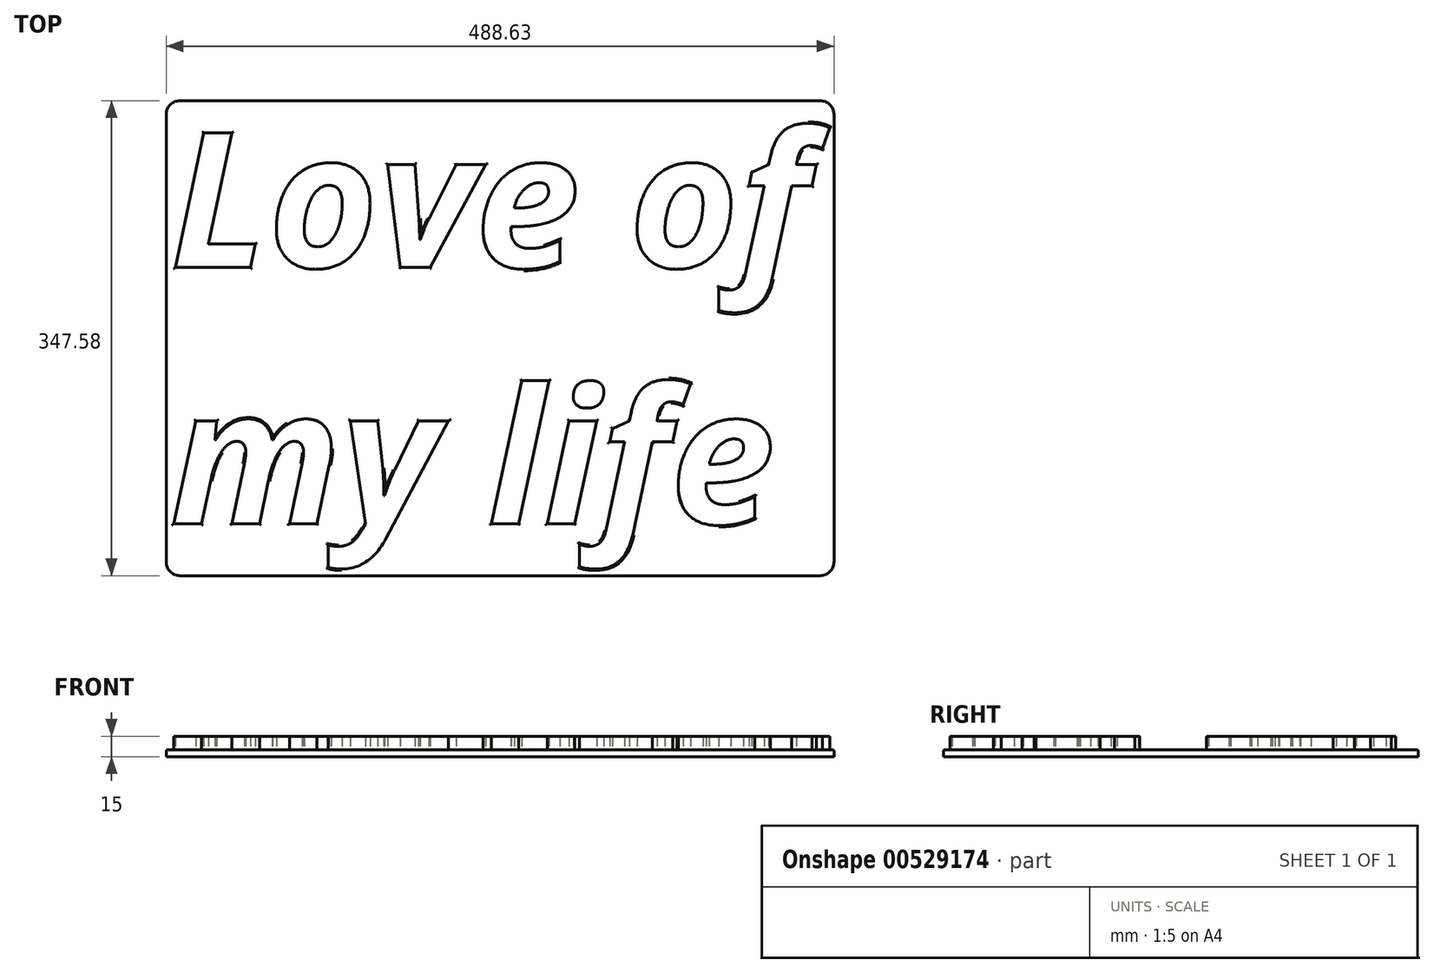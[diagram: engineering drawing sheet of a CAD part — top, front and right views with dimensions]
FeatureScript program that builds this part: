
annotation { "Feature Type Name" : "Feature", "Feature Type Description" : "" }
export const myFeature = defineFeature(function(context is Context, id is Id, definition is map)
    precondition{}
    {
        {
            var Q0;
            Q0=qCreatedBy(makeId("Top.planeOp"),FACE);
            var sketch = newSketch(context, id + "F0", { "sketchPlane" : qUnion([Q0])});
            skText(sketch, "E0", { "text": "Love of \nmy life", "fontName": "OpenSans-BoldItalic.ttf"});
            const initialGuessF0  = {"E0": [-0.07003, -0.04766, 1, 0, 0.09928]};
            skSetInitialGuess(sketch, initialGuessF0);
            skSolve(sketch);
        }
        {
            var Q0;
            Q0 = qSketchRegion(id + "F0", true);
            extrude(context, id + "F1", {"entities" : qUnion([Q0]), "depth" : 10 * mm, "offsetDistance" : 25 * mm});
        }
        {
            var Q0;
            Q0=qCreatedBy(makeId("Top.planeOp"),FACE);
            var sketch = newSketch(context, id + "F2", { "sketchPlane" : qUnion([Q0])});
            skLineSegment(sketch, "E1.bottom", {"start": v(-73.16, 74.37) * mm, "end": v(415.47, 74.37) * mm});
            skLineSegment(sketch, "E1.top", {"start": v(-73.16, -273.2) * mm, "end": v(415.47, -273.2) * mm});
            skLineSegment(sketch, "E1.left", {"start": v(-73.16, 74.37) * mm, "end": v(-73.16, -273.2) * mm});
            skLineSegment(sketch, "E1.right", {"start": v(415.47, 74.37) * mm, "end": v(415.47, -273.2) * mm});
            skSolve(sketch);
        }
        {
            var Q0;
            Q0 = qSketchRegion(id + "F2", true);
            extrude(context, id + "F3", {"entities" : qUnion([Q0]), "oppositeDirection" : true, "depth" : 5 * mm, "offsetDistance" : 25 * mm});
        }
        {
            var Q0;
            Q0=makeQuery(id+"F1.opExtrude","SWEPT_BODY",BODY,{"disambiguationData":[OSD([sQuery(id+"F0.wireOp",EDGE,"E0.sketch_text.stroke-0"),sQuery(id+"F0.wireOp",EDGE,"E0.sketch_text.stroke-1"),sQuery(id+"F0.wireOp",EDGE,"E0.sketch_text.stroke-2"),sQuery(id+"F0.wireOp",EDGE,"E0.sketch_text.stroke-3"),sQuery(id+"F0.wireOp",EDGE,"E0.sketch_text.stroke-4"),sQuery(id+"F0.wireOp",EDGE,"E0.sketch_text.stroke-5")])]});
            var Q1;
            Q1=makeQuery(id+"F1.opExtrude","SWEPT_BODY",BODY,{"disambiguationData":[OSD([sQuery(id+"F0.wireOp",EDGE,"E0.sketch_text.stroke-6"),sQuery(id+"F0.wireOp",EDGE,"E0.sketch_text.stroke-7"),sQuery(id+"F0.wireOp",EDGE,"E0.sketch_text.stroke-8"),sQuery(id+"F0.wireOp",EDGE,"E0.sketch_text.stroke-9"),sQuery(id+"F0.wireOp",EDGE,"E0.sketch_text.stroke-10"),sQuery(id+"F0.wireOp",EDGE,"E0.sketch_text.stroke-11"),sQuery(id+"F0.wireOp",EDGE,"E0.sketch_text.stroke-12"),sQuery(id+"F0.wireOp",EDGE,"E0.sketch_text.stroke-13"),sQuery(id+"F0.wireOp",EDGE,"E0.sketch_text.stroke-14"),sQuery(id+"F0.wireOp",EDGE,"E0.sketch_text.stroke-15"),sQuery(id+"F0.wireOp",EDGE,"E0.sketch_text.stroke-16"),sQuery(id+"F0.wireOp",EDGE,"E0.sketch_text.stroke-17"),sQuery(id+"F0.wireOp",EDGE,"E0.sketch_text.stroke-18"),sQuery(id+"F0.wireOp",EDGE,"E0.sketch_text.stroke-19"),sQuery(id+"F0.wireOp",EDGE,"E0.sketch_text.stroke-20"),sQuery(id+"F0.wireOp",EDGE,"E0.sketch_text.stroke-21"),sQuery(id+"F0.wireOp",EDGE,"E0.sketch_text.stroke-22"),sQuery(id+"F0.wireOp",EDGE,"E0.sketch_text.stroke-23")])]});
            var Q2;
            Q2=makeQuery(id+"F1.opExtrude","SWEPT_BODY",BODY,{"disambiguationData":[OSD([sQuery(id+"F0.wireOp",EDGE,"E0.sketch_text.stroke-24"),sQuery(id+"F0.wireOp",EDGE,"E0.sketch_text.stroke-25"),sQuery(id+"F0.wireOp",EDGE,"E0.sketch_text.stroke-26"),sQuery(id+"F0.wireOp",EDGE,"E0.sketch_text.stroke-27"),sQuery(id+"F0.wireOp",EDGE,"E0.sketch_text.stroke-28"),sQuery(id+"F0.wireOp",EDGE,"E0.sketch_text.stroke-29"),sQuery(id+"F0.wireOp",EDGE,"E0.sketch_text.stroke-30"),sQuery(id+"F0.wireOp",EDGE,"E0.sketch_text.stroke-31"),sQuery(id+"F0.wireOp",EDGE,"E0.sketch_text.stroke-32"),sQuery(id+"F0.wireOp",EDGE,"E0.sketch_text.stroke-33")])]});
            var Q3;
            Q3=makeQuery(id+"F1.opExtrude","SWEPT_BODY",BODY,{"disambiguationData":[OSD([sQuery(id+"F0.wireOp",EDGE,"E0.sketch_text.stroke-34"),sQuery(id+"F0.wireOp",EDGE,"E0.sketch_text.stroke-35"),sQuery(id+"F0.wireOp",EDGE,"E0.sketch_text.stroke-36"),sQuery(id+"F0.wireOp",EDGE,"E0.sketch_text.stroke-37"),sQuery(id+"F0.wireOp",EDGE,"E0.sketch_text.stroke-38"),sQuery(id+"F0.wireOp",EDGE,"E0.sketch_text.stroke-39"),sQuery(id+"F0.wireOp",EDGE,"E0.sketch_text.stroke-40"),sQuery(id+"F0.wireOp",EDGE,"E0.sketch_text.stroke-41"),sQuery(id+"F0.wireOp",EDGE,"E0.sketch_text.stroke-42"),sQuery(id+"F0.wireOp",EDGE,"E0.sketch_text.stroke-43"),sQuery(id+"F0.wireOp",EDGE,"E0.sketch_text.stroke-44"),sQuery(id+"F0.wireOp",EDGE,"E0.sketch_text.stroke-45"),sQuery(id+"F0.wireOp",EDGE,"E0.sketch_text.stroke-46"),sQuery(id+"F0.wireOp",EDGE,"E0.sketch_text.stroke-47"),sQuery(id+"F0.wireOp",EDGE,"E0.sketch_text.stroke-48"),sQuery(id+"F0.wireOp",EDGE,"E0.sketch_text.stroke-49"),sQuery(id+"F0.wireOp",EDGE,"E0.sketch_text.stroke-50"),sQuery(id+"F0.wireOp",EDGE,"E0.sketch_text.stroke-51"),sQuery(id+"F0.wireOp",EDGE,"E0.sketch_text.stroke-52"),sQuery(id+"F0.wireOp",EDGE,"E0.sketch_text.stroke-53"),sQuery(id+"F0.wireOp",EDGE,"E0.sketch_text.stroke-54"),sQuery(id+"F0.wireOp",EDGE,"E0.sketch_text.stroke-55"),sQuery(id+"F0.wireOp",EDGE,"E0.sketch_text.stroke-56"),sQuery(id+"F0.wireOp",EDGE,"E0.sketch_text.stroke-57")])]});
            var Q4;
            Q4=makeQuery(id+"F1.opExtrude","SWEPT_BODY",BODY,{"disambiguationData":[OSD([sQuery(id+"F0.wireOp",EDGE,"E0.sketch_text.stroke-58"),sQuery(id+"F0.wireOp",EDGE,"E0.sketch_text.stroke-59"),sQuery(id+"F0.wireOp",EDGE,"E0.sketch_text.stroke-60"),sQuery(id+"F0.wireOp",EDGE,"E0.sketch_text.stroke-61"),sQuery(id+"F0.wireOp",EDGE,"E0.sketch_text.stroke-62"),sQuery(id+"F0.wireOp",EDGE,"E0.sketch_text.stroke-63"),sQuery(id+"F0.wireOp",EDGE,"E0.sketch_text.stroke-64"),sQuery(id+"F0.wireOp",EDGE,"E0.sketch_text.stroke-65"),sQuery(id+"F0.wireOp",EDGE,"E0.sketch_text.stroke-66"),sQuery(id+"F0.wireOp",EDGE,"E0.sketch_text.stroke-67"),sQuery(id+"F0.wireOp",EDGE,"E0.sketch_text.stroke-68"),sQuery(id+"F0.wireOp",EDGE,"E0.sketch_text.stroke-69"),sQuery(id+"F0.wireOp",EDGE,"E0.sketch_text.stroke-70"),sQuery(id+"F0.wireOp",EDGE,"E0.sketch_text.stroke-71"),sQuery(id+"F0.wireOp",EDGE,"E0.sketch_text.stroke-72"),sQuery(id+"F0.wireOp",EDGE,"E0.sketch_text.stroke-73"),sQuery(id+"F0.wireOp",EDGE,"E0.sketch_text.stroke-74"),sQuery(id+"F0.wireOp",EDGE,"E0.sketch_text.stroke-75")])]});
            var Q5;
            Q5=makeQuery(id+"F1.opExtrude","SWEPT_BODY",BODY,{"disambiguationData":[OSD([sQuery(id+"F0.wireOp",EDGE,"E0.sketch_text.stroke-76"),sQuery(id+"F0.wireOp",EDGE,"E0.sketch_text.stroke-77"),sQuery(id+"F0.wireOp",EDGE,"E0.sketch_text.stroke-78"),sQuery(id+"F0.wireOp",EDGE,"E0.sketch_text.stroke-79"),sQuery(id+"F0.wireOp",EDGE,"E0.sketch_text.stroke-80"),sQuery(id+"F0.wireOp",EDGE,"E0.sketch_text.stroke-81"),sQuery(id+"F0.wireOp",EDGE,"E0.sketch_text.stroke-82"),sQuery(id+"F0.wireOp",EDGE,"E0.sketch_text.stroke-83"),sQuery(id+"F0.wireOp",EDGE,"E0.sketch_text.stroke-84"),sQuery(id+"F0.wireOp",EDGE,"E0.sketch_text.stroke-85"),sQuery(id+"F0.wireOp",EDGE,"E0.sketch_text.stroke-86"),sQuery(id+"F0.wireOp",EDGE,"E0.sketch_text.stroke-87"),sQuery(id+"F0.wireOp",EDGE,"E0.sketch_text.stroke-88"),sQuery(id+"F0.wireOp",EDGE,"E0.sketch_text.stroke-89"),sQuery(id+"F0.wireOp",EDGE,"E0.sketch_text.stroke-90"),sQuery(id+"F0.wireOp",EDGE,"E0.sketch_text.stroke-91"),sQuery(id+"F0.wireOp",EDGE,"E0.sketch_text.stroke-92"),sQuery(id+"F0.wireOp",EDGE,"E0.sketch_text.stroke-93"),sQuery(id+"F0.wireOp",EDGE,"E0.sketch_text.stroke-94"),sQuery(id+"F0.wireOp",EDGE,"E0.sketch_text.stroke-95"),sQuery(id+"F0.wireOp",EDGE,"E0.sketch_text.stroke-96"),sQuery(id+"F0.wireOp",EDGE,"E0.sketch_text.stroke-97"),sQuery(id+"F0.wireOp",EDGE,"E0.sketch_text.stroke-98")])]});
            var Q6;
            Q6=makeQuery(id+"F1.opExtrude","SWEPT_BODY",BODY,{"disambiguationData":[OSD([sQuery(id+"F0.wireOp",EDGE,"E0.sketch_text.stroke-99"),sQuery(id+"F0.wireOp",EDGE,"E0.sketch_text.stroke-100"),sQuery(id+"F0.wireOp",EDGE,"E0.sketch_text.stroke-101"),sQuery(id+"F0.wireOp",EDGE,"E0.sketch_text.stroke-102"),sQuery(id+"F0.wireOp",EDGE,"E0.sketch_text.stroke-103"),sQuery(id+"F0.wireOp",EDGE,"E0.sketch_text.stroke-104"),sQuery(id+"F0.wireOp",EDGE,"E0.sketch_text.stroke-105"),sQuery(id+"F0.wireOp",EDGE,"E0.sketch_text.stroke-106"),sQuery(id+"F0.wireOp",EDGE,"E0.sketch_text.stroke-107"),sQuery(id+"F0.wireOp",EDGE,"E0.sketch_text.stroke-108"),sQuery(id+"F0.wireOp",EDGE,"E0.sketch_text.stroke-109"),sQuery(id+"F0.wireOp",EDGE,"E0.sketch_text.stroke-110"),sQuery(id+"F0.wireOp",EDGE,"E0.sketch_text.stroke-111"),sQuery(id+"F0.wireOp",EDGE,"E0.sketch_text.stroke-112"),sQuery(id+"F0.wireOp",EDGE,"E0.sketch_text.stroke-113"),sQuery(id+"F0.wireOp",EDGE,"E0.sketch_text.stroke-114"),sQuery(id+"F0.wireOp",EDGE,"E0.sketch_text.stroke-115"),sQuery(id+"F0.wireOp",EDGE,"E0.sketch_text.stroke-116"),sQuery(id+"F0.wireOp",EDGE,"E0.sketch_text.stroke-117"),sQuery(id+"F0.wireOp",EDGE,"E0.sketch_text.stroke-118"),sQuery(id+"F0.wireOp",EDGE,"E0.sketch_text.stroke-119"),sQuery(id+"F0.wireOp",EDGE,"E0.sketch_text.stroke-120"),sQuery(id+"F0.wireOp",EDGE,"E0.sketch_text.stroke-121"),sQuery(id+"F0.wireOp",EDGE,"E0.sketch_text.stroke-122"),sQuery(id+"F0.wireOp",EDGE,"E0.sketch_text.stroke-123"),sQuery(id+"F0.wireOp",EDGE,"E0.sketch_text.stroke-124"),sQuery(id+"F0.wireOp",EDGE,"E0.sketch_text.stroke-125"),sQuery(id+"F0.wireOp",EDGE,"E0.sketch_text.stroke-126")])]});
            var Q7;
            Q7=makeQuery(id+"F1.opExtrude","SWEPT_BODY",BODY,{"disambiguationData":[OSD([sQuery(id+"F0.wireOp",EDGE,"E0.sketch_text.stroke-127"),sQuery(id+"F0.wireOp",EDGE,"E0.sketch_text.stroke-128"),sQuery(id+"F0.wireOp",EDGE,"E0.sketch_text.stroke-129"),sQuery(id+"F0.wireOp",EDGE,"E0.sketch_text.stroke-130"),sQuery(id+"F0.wireOp",EDGE,"E0.sketch_text.stroke-131"),sQuery(id+"F0.wireOp",EDGE,"E0.sketch_text.stroke-132"),sQuery(id+"F0.wireOp",EDGE,"E0.sketch_text.stroke-133"),sQuery(id+"F0.wireOp",EDGE,"E0.sketch_text.stroke-134"),sQuery(id+"F0.wireOp",EDGE,"E0.sketch_text.stroke-135"),sQuery(id+"F0.wireOp",EDGE,"E0.sketch_text.stroke-136"),sQuery(id+"F0.wireOp",EDGE,"E0.sketch_text.stroke-137"),sQuery(id+"F0.wireOp",EDGE,"E0.sketch_text.stroke-138"),sQuery(id+"F0.wireOp",EDGE,"E0.sketch_text.stroke-139"),sQuery(id+"F0.wireOp",EDGE,"E0.sketch_text.stroke-140"),sQuery(id+"F0.wireOp",EDGE,"E0.sketch_text.stroke-141"),sQuery(id+"F0.wireOp",EDGE,"E0.sketch_text.stroke-142"),sQuery(id+"F0.wireOp",EDGE,"E0.sketch_text.stroke-143")])]});
            var Q8;
            Q8=makeQuery(id+"F1.opExtrude","SWEPT_BODY",BODY,{"disambiguationData":[OSD([sQuery(id+"F0.wireOp",EDGE,"E0.sketch_text.stroke-144"),sQuery(id+"F0.wireOp",EDGE,"E0.sketch_text.stroke-145"),sQuery(id+"F0.wireOp",EDGE,"E0.sketch_text.stroke-146"),sQuery(id+"F0.wireOp",EDGE,"E0.sketch_text.stroke-147")])]});
            var Q9;
            Q9=makeQuery(id+"F1.opExtrude","SWEPT_BODY",BODY,{"disambiguationData":[OSD([sQuery(id+"F0.wireOp",EDGE,"E0.sketch_text.stroke-148"),sQuery(id+"F0.wireOp",EDGE,"E0.sketch_text.stroke-149"),sQuery(id+"F0.wireOp",EDGE,"E0.sketch_text.stroke-150"),sQuery(id+"F0.wireOp",EDGE,"E0.sketch_text.stroke-151"),sQuery(id+"F0.wireOp",EDGE,"E0.sketch_text.stroke-152"),sQuery(id+"F0.wireOp",EDGE,"E0.sketch_text.stroke-153"),sQuery(id+"F0.wireOp",EDGE,"E0.sketch_text.stroke-154")])]});
            var Q10;
            Q10=makeQuery(id+"F1.opExtrude","SWEPT_BODY",BODY,{"disambiguationData":[OSD([sQuery(id+"F0.wireOp",EDGE,"E0.sketch_text.stroke-155"),sQuery(id+"F0.wireOp",EDGE,"E0.sketch_text.stroke-156"),sQuery(id+"F0.wireOp",EDGE,"E0.sketch_text.stroke-157"),sQuery(id+"F0.wireOp",EDGE,"E0.sketch_text.stroke-158")])]});
            var Q11;
            Q11=makeQuery(id+"F1.opExtrude","SWEPT_BODY",BODY,{"disambiguationData":[OSD([sQuery(id+"F0.wireOp",EDGE,"E0.sketch_text.stroke-159"),sQuery(id+"F0.wireOp",EDGE,"E0.sketch_text.stroke-160"),sQuery(id+"F0.wireOp",EDGE,"E0.sketch_text.stroke-161"),sQuery(id+"F0.wireOp",EDGE,"E0.sketch_text.stroke-162"),sQuery(id+"F0.wireOp",EDGE,"E0.sketch_text.stroke-163"),sQuery(id+"F0.wireOp",EDGE,"E0.sketch_text.stroke-164"),sQuery(id+"F0.wireOp",EDGE,"E0.sketch_text.stroke-165"),sQuery(id+"F0.wireOp",EDGE,"E0.sketch_text.stroke-166"),sQuery(id+"F0.wireOp",EDGE,"E0.sketch_text.stroke-167"),sQuery(id+"F0.wireOp",EDGE,"E0.sketch_text.stroke-168"),sQuery(id+"F0.wireOp",EDGE,"E0.sketch_text.stroke-169"),sQuery(id+"F0.wireOp",EDGE,"E0.sketch_text.stroke-170"),sQuery(id+"F0.wireOp",EDGE,"E0.sketch_text.stroke-171"),sQuery(id+"F0.wireOp",EDGE,"E0.sketch_text.stroke-172"),sQuery(id+"F0.wireOp",EDGE,"E0.sketch_text.stroke-173"),sQuery(id+"F0.wireOp",EDGE,"E0.sketch_text.stroke-174"),sQuery(id+"F0.wireOp",EDGE,"E0.sketch_text.stroke-175"),sQuery(id+"F0.wireOp",EDGE,"E0.sketch_text.stroke-176"),sQuery(id+"F0.wireOp",EDGE,"E0.sketch_text.stroke-177"),sQuery(id+"F0.wireOp",EDGE,"E0.sketch_text.stroke-178"),sQuery(id+"F0.wireOp",EDGE,"E0.sketch_text.stroke-179"),sQuery(id+"F0.wireOp",EDGE,"E0.sketch_text.stroke-180"),sQuery(id+"F0.wireOp",EDGE,"E0.sketch_text.stroke-181")])]});
            var Q12;
            Q12=makeQuery(id+"F1.opExtrude","SWEPT_BODY",BODY,{"disambiguationData":[OSD([sQuery(id+"F0.wireOp",EDGE,"E0.sketch_text.stroke-182"),sQuery(id+"F0.wireOp",EDGE,"E0.sketch_text.stroke-183"),sQuery(id+"F0.wireOp",EDGE,"E0.sketch_text.stroke-184"),sQuery(id+"F0.wireOp",EDGE,"E0.sketch_text.stroke-185"),sQuery(id+"F0.wireOp",EDGE,"E0.sketch_text.stroke-186"),sQuery(id+"F0.wireOp",EDGE,"E0.sketch_text.stroke-187"),sQuery(id+"F0.wireOp",EDGE,"E0.sketch_text.stroke-188"),sQuery(id+"F0.wireOp",EDGE,"E0.sketch_text.stroke-189"),sQuery(id+"F0.wireOp",EDGE,"E0.sketch_text.stroke-190"),sQuery(id+"F0.wireOp",EDGE,"E0.sketch_text.stroke-191"),sQuery(id+"F0.wireOp",EDGE,"E0.sketch_text.stroke-192"),sQuery(id+"F0.wireOp",EDGE,"E0.sketch_text.stroke-193"),sQuery(id+"F0.wireOp",EDGE,"E0.sketch_text.stroke-194"),sQuery(id+"F0.wireOp",EDGE,"E0.sketch_text.stroke-195"),sQuery(id+"F0.wireOp",EDGE,"E0.sketch_text.stroke-196"),sQuery(id+"F0.wireOp",EDGE,"E0.sketch_text.stroke-197"),sQuery(id+"F0.wireOp",EDGE,"E0.sketch_text.stroke-198"),sQuery(id+"F0.wireOp",EDGE,"E0.sketch_text.stroke-199"),sQuery(id+"F0.wireOp",EDGE,"E0.sketch_text.stroke-200"),sQuery(id+"F0.wireOp",EDGE,"E0.sketch_text.stroke-201"),sQuery(id+"F0.wireOp",EDGE,"E0.sketch_text.stroke-202"),sQuery(id+"F0.wireOp",EDGE,"E0.sketch_text.stroke-203"),sQuery(id+"F0.wireOp",EDGE,"E0.sketch_text.stroke-204"),sQuery(id+"F0.wireOp",EDGE,"E0.sketch_text.stroke-205")])]});
            var Q13;
            Q13=makeQuery(id+"F3.opExtrude","SWEPT_BODY",BODY,{"disambiguationData":[OSD([sQuery(id+"F2.wireOp",EDGE,"E1.bottom"),sQuery(id+"F2.wireOp",EDGE,"E1.top"),sQuery(id+"F2.wireOp",EDGE,"E1.left"),sQuery(id+"F2.wireOp",EDGE,"E1.right")])]});
            booleanBodies(context, id + "F4", {"operationType" : BooleanOperationType.UNION, "tools" : qUnion([Q0, Q1, Q2, Q3, Q4, Q5, Q6, Q7, Q8, Q9, Q10, Q11, Q12, Q13])});
        }
        {
            var Q0;
            Q0=makeQuery(id+"F3.opExtrude","SWEPT_EDGE",EDGE,{"disambiguationData":[OSD([sQuery(id+"F2.wireOp",EDGE,"E1.bottom"),sQuery(id+"F2.wireOp",EDGE,"E1.left")])]});
            var Q1;
            Q1=makeQuery(id+"F3.opExtrude","SWEPT_EDGE",EDGE,{"disambiguationData":[OSD([sQuery(id+"F2.wireOp",EDGE,"E1.top"),sQuery(id+"F2.wireOp",EDGE,"E1.left")])]});
            var Q2;
            Q2=makeQuery(id+"F3.opExtrude","SWEPT_EDGE",EDGE,{"disambiguationData":[OSD([sQuery(id+"F2.wireOp",EDGE,"E1.top"),sQuery(id+"F2.wireOp",EDGE,"E1.right")])]});
            var Q3;
            Q3=makeQuery(id+"F3.opExtrude","SWEPT_EDGE",EDGE,{"disambiguationData":[OSD([sQuery(id+"F2.wireOp",EDGE,"E1.bottom"),sQuery(id+"F2.wireOp",EDGE,"E1.right")])]});
            fillet(context, id + "F5", {"entities" : qUnion([Q0, Q1, Q2, Q3]), "radius" : 10 * mm, "tangentPropagation" : true, "allowEdgeOverflow" : false});
        }
        {
            var Q0;
            {var subQ0=sQuery(id+"F2.wireOp",EDGE,"E1.right");var subQ1=sQuery(id+"F2.wireOp",EDGE,"E1.left");var subQ2=sQuery(id+"F2.wireOp",EDGE,"E1.bottom");var subQ3=sQuery(id+"F2.wireOp",EDGE,"E1.top");Q0=makeQuery(id+"F4.opBoolean","SPLIT",FACE,{"disambiguationData":[TD([makeQuery(id+"F1.opExtrude","SWEPT_FACE",FACE,{"disambiguationData":[OSD([sQuery(id+"F0.wireOp",EDGE,"E0.sketch_text.stroke-0")])]})])],"derivedFrom":makeQuery(id+"F3.opExtrude","CAP_FACE",FACE,{"disambiguationData":[OSD([subQ2,subQ3,subQ1,subQ0])],"isStart":true})});}
            fillet(context, id + "F6", {"entities" : qUnion([Q0]), "radius" : 1 * mm, "tangentPropagation" : true, "allowEdgeOverflow" : false});
        }
    });
